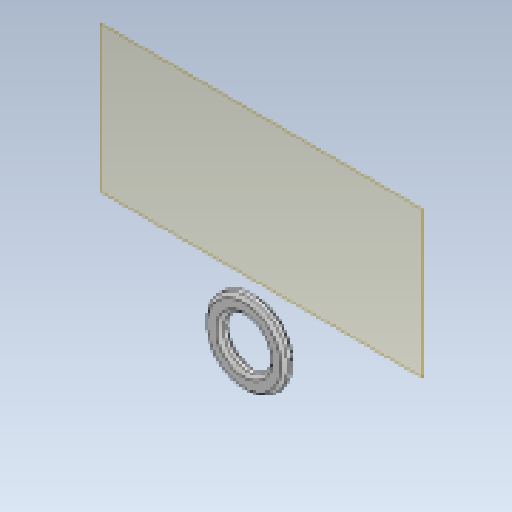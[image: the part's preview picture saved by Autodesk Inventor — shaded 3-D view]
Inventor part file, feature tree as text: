
AUTODESK INVENTOR PART (.ipt)
format: ipt  version: 2023 (Build 270158030, 158C)  size: 117,248 bytes
history: native  units: mm
features: other x4, chamfer x2, reference x2, plane x1, extrude x1, sketch x1
ambient origin geometry x8: Origin, YZ Plane, XZ Plane, XY Plane, X Axis, Y Axis, Z Axis, Center Point
bodies: Body1 (feature_tree)
feature tree (11):
  other  "washer"
  plane  "Work Plane1"
  extrude  "Extrusion1"  Depth=1.6mm TaperAngle=0.0deg
  chamfer  "Chamfer1"  Distance=0.5mm Angle=45.0deg
  chamfer  "Chamfer2"  Distance=6.4mm
  sketch  "Sketch1"  dims[d0=1.8mm d1=1.6mm d2=0.0mm d3=0.5mm d4=2.0mm d5=45.0deg d6=6.4mm d7=0.5mm d8=2.0mm d9=45.0deg]
  reference  "Reference1"
  reference  "Reference2"
  other  "<userpath>\Documents\0004-inventor\3D-CAD-main\trebuchet\trebuchet-assembly.iam"
  other  "trebuchet-assembly.iam"
  other  "v1-counterweight:1"
